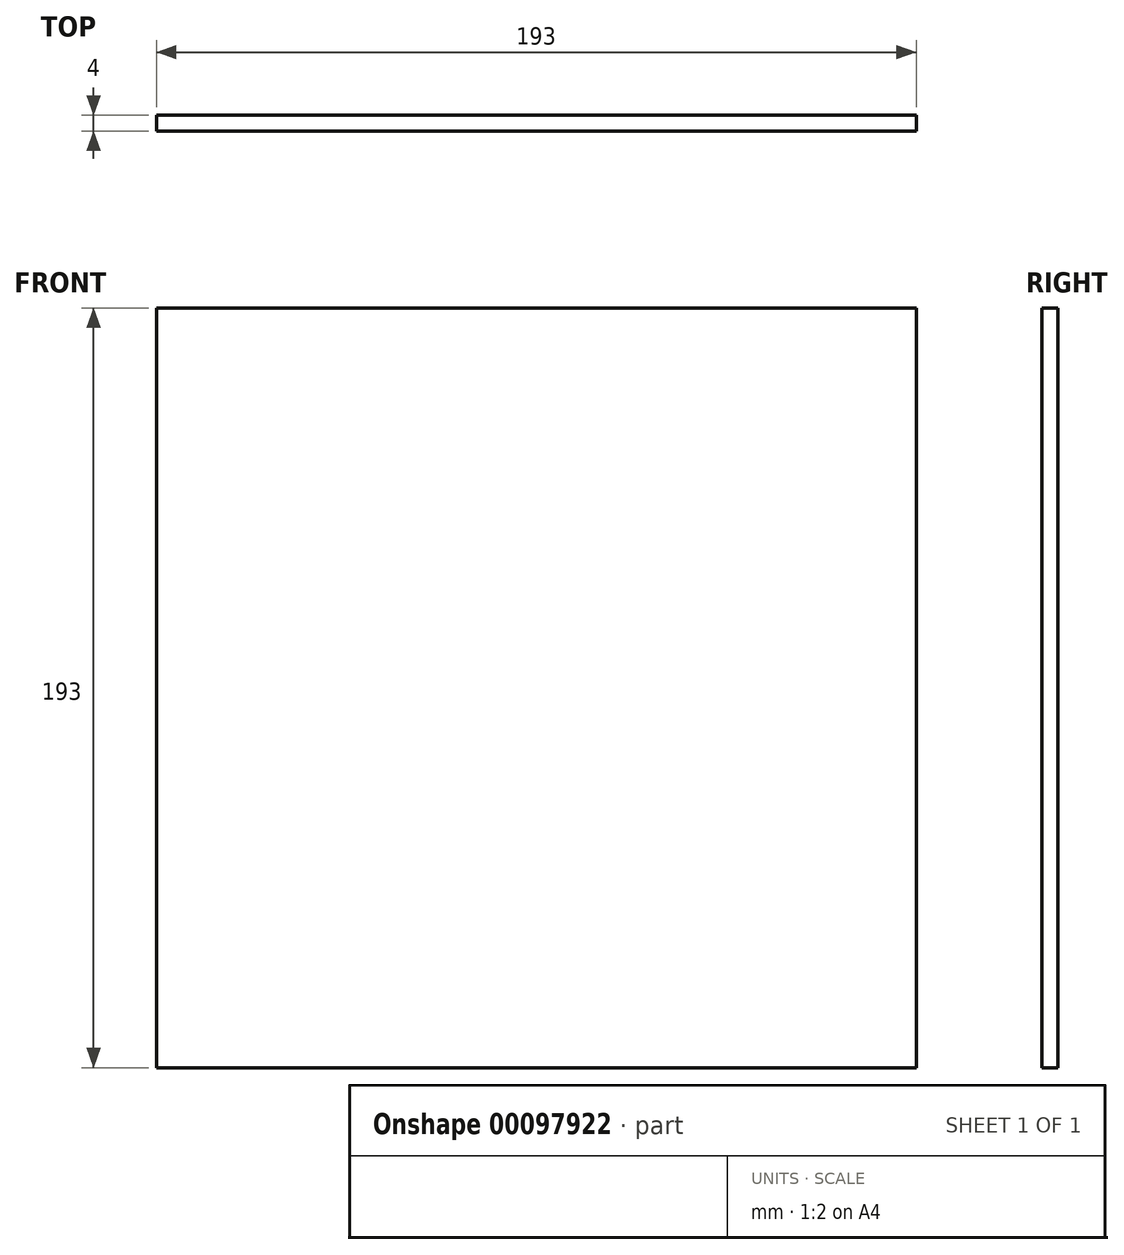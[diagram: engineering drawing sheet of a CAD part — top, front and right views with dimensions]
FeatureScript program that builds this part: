
annotation { "Feature Type Name" : "Feature", "Feature Type Description" : "" }
export const myFeature = defineFeature(function(context is Context, id is Id, definition is map)
    precondition{}
    {
        {
            var Q0;
            Q0=qCreatedBy(makeId("Front.planeOp"),FACE);
            var sketch = newSketch(context, id + "F0", { "sketchPlane" : qUnion([Q0])});
            skLineSegment(sketch, "E0.bottom", {"start": v(-96.5, 96.5) * mm, "end": v(96.5, 96.5) * mm});
            skLineSegment(sketch, "E0.top", {"start": v(-96.5, -96.5) * mm, "end": v(96.5, -96.5) * mm});
            skLineSegment(sketch, "E0.left", {"start": v(-96.5, 96.5) * mm, "end": v(-96.5, -96.5) * mm});
            skLineSegment(sketch, "E0.right", {"start": v(96.5, 96.5) * mm, "end": v(96.5, -96.5) * mm});
            skSolve(sketch);
        }
        {
            var Q0;
            Q0=makeQuery(id+"F0.imprint","IMPRINT",FACE,{"disambiguationData":[TD([[makeQuery(id+"F0.imprint","IMPRINT",EDGE,{"derivedFrom":sQuery(id+"F0.wireOp",EDGE,"E0.bottom")}),-1.0]])]});
            extrude(context, id + "F1", {"entities" : qUnion([Q0]), "depth" : 4 * mm});
        }
    });
